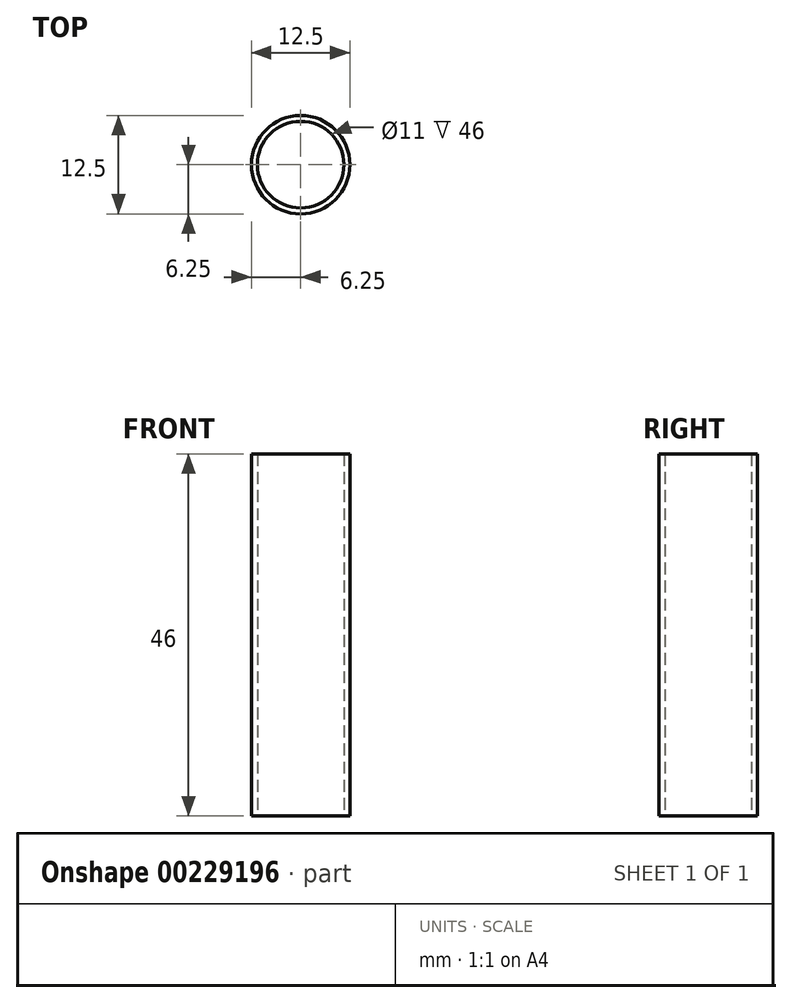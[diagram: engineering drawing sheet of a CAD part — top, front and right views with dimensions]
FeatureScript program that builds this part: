
annotation { "Feature Type Name" : "Feature", "Feature Type Description" : "" }
export const myFeature = defineFeature(function(context is Context, id is Id, definition is map)
    precondition{}
    {
        {
            var Q0;
            Q0=qCreatedBy(makeId("Top.planeOp"),FACE);
            var sketch = newSketch(context, id + "F0", { "sketchPlane" : qUnion([Q0])});
            skCircle(sketch, "E0", {"center": v(0, 0) * mm, "radius": 6.25 * mm});
            skCircle(sketch, "E1", {"center": v(0, 0) * mm, "radius": 5.5 * mm});
            skSolve(sketch);
        }
        {
            var Q0;
            Q0 = qSketchRegion(id + "F0", true);
            extrude(context, id + "F1", {"entities" : qUnion([Q0]), "depth" : 46 * mm});
        }
    });
